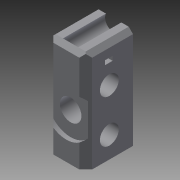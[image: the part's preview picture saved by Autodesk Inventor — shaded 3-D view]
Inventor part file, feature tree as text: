
AUTODESK INVENTOR PART (.ipt)
format: ipt  version: 2015 (Build 190159000, 159)  size: 158,720 bytes
history: native  units: mm
features: sketch x6, chamfer x5, extrude x3, hole x3
ambient origin geometry x8: Origin, YZ Plane, XZ Plane, XY Plane, X Axis, Y Axis, Z Axis, Center Point
bodies: Solid1 (feature_tree)
feature tree (17):
  extrude  "Extrusion1"  Depth=22.0mm
  hole  "Hole3"  [1 undecoded]
  hole  "Hole4"  [1 undecoded]
  chamfer  "Chamfer1"  Distance=2.0mm Angle=45.0deg
  chamfer  "Chamfer2"  Distance=2.0mm Angle=45.0deg
  chamfer  "Chamfer3"  Distance=2.0mm Angle=45.0deg
  chamfer  "Chamfer4"  Distance=2.0mm Angle=45.0deg
  chamfer  "Chamfer5"  Distance=2.0mm Angle=45.0deg
  hole  "Hole5"  [1 undecoded]
  extrude  "Extrusion4"  Depth=3.5mm
  extrude  "Extrusion5"  Depth=6.0mm
  sketch  "Sketch1"  dims[d0=18.0mm d1=22.0mm]
  sketch  "Sketch3"  dims[d2=47.0mm d3=0.0mm]
  sketch  "Sketch4"  dims[d22=8.0mm d23=6.0mm d24=4.0mm d25=2.0mm d26=90.0deg d27=20.0mm d28=0.0mm d31=1.8mm]
  sketch  "Sketch6"  dims[d33=17.0mm]
  sketch  "Sketch7"  dims[d34=8.8mm d35=6.0mm d36=4.0mm d37=2.0mm d38=90.0deg d39=8.0mm d40=20.594885mm d42=20.0mm d43=3.0mm d44=2.0mm d45=45.0deg d46=3.0mm d47=2.0mm d48=45.0deg d49=2.0mm d50=2.0mm d51=45.0deg d52=2.0mm d53=2.0mm d54=45.0deg d55=2.0mm d56=2.0mm d57=45.0deg]
  sketch  "Sketch8"  dims[d67=20.0mm d68=10.0mm d69=6.0mm d70=22.0mm d71=2.0mm d72=90.0deg d73=8.0mm d74=20.594885mm d75=2.0mm d76=3.5mm d77=6.0mm d78=9.0mm d79=10.0mm d80=0.0mm d81=2.0mm d82=3.5mm d83=9.0mm d85=8.0mm d86=8.0mm d87=0.0mm]
note: 3 required parameter values undecoded (feature->parameter linkage not recoverable at this tier; creation-order binding heuristic only, values carry confidence <= 0.55)
